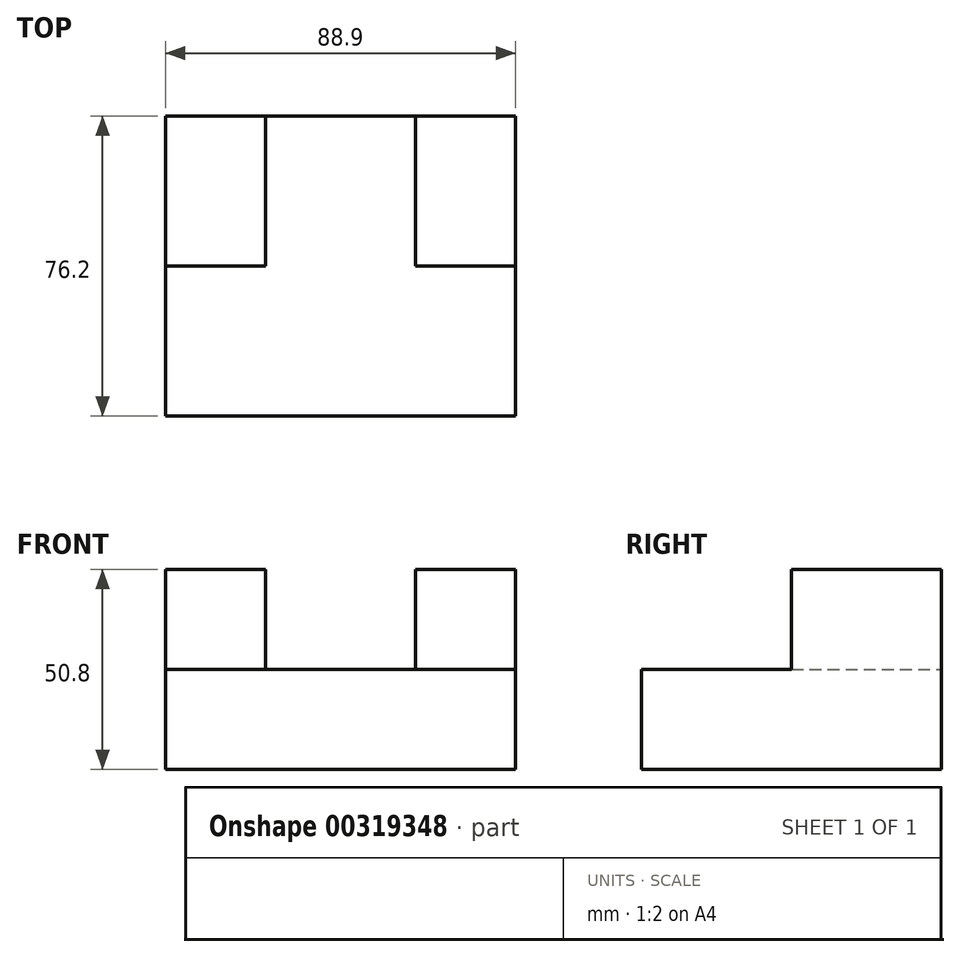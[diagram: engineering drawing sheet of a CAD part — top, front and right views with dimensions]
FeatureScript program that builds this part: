
annotation { "Feature Type Name" : "Feature", "Feature Type Description" : "" }
export const myFeature = defineFeature(function(context is Context, id is Id, definition is map)
    precondition{}
    {
        {
            var Q0;
            Q0=qCreatedBy(makeId("Front.planeOp"),FACE);
            var sketch = newSketch(context, id + "F0", { "sketchPlane" : qUnion([Q0])});
            skLineSegment(sketch, "E0", {"start": v(-56.68, -59.75) * mm, "end": v(32.22, -59.75) * mm});
            skLineSegment(sketch, "E1", {"start": v(32.22, -59.75) * mm, "end": v(32.22, -34.35) * mm});
            skLineSegment(sketch, "E2", {"start": v(-56.68, -59.75) * mm, "end": v(-56.68, -34.35) * mm});
            skLineSegment(sketch, "E3", {"start": v(-56.68, -34.35) * mm, "end": v(32.22, -34.35) * mm});
            skSolve(sketch);
        }
        {
            var Q0;
            Q0 = qSketchRegion(id + "F0", true);
            extrude(context, id + "F1", {"entities" : qUnion([Q0]), "depth" : 76.2 * mm});
        }
        {
            var Q0;
            Q0=makeQuery(id+"F1.opExtrude","SWEPT_FACE",FACE,{"disambiguationData":[OSD([sQuery(id+"F0.wireOp",EDGE,"E3")])]});
            var sketch = newSketch(context, id + "F2", { "sketchPlane" : qUnion([Q0])});
            skLineSegment(sketch, "E4", {"start": v(-56.68, 0) * mm, "end": v(-56.68, -38.1) * mm});
            skLineSegment(sketch, "E5", {"start": v(-56.68, -38.1) * mm, "end": v(-31.28, -38.1) * mm});
            skLineSegment(sketch, "E6", {"start": v(-31.28, -38.1) * mm, "end": v(-31.28, 0) * mm});
            skLineSegment(sketch, "E7", {"start": v(32.22, -38.1) * mm, "end": v(6.82, -38.1) * mm});
            skLineSegment(sketch, "E8", {"start": v(6.82, -38.1) * mm, "end": v(6.82, 0) * mm});
            skSolve(sketch);
        }
        {
            var Q0;
            {var subQ0=sQuery(id+"F2.wireOp",EDGE,"E4");Q0=makeQuery(id+"F2.imprint","IMPRINT",FACE,{"disambiguationData":[TD([[makeQuery(id+"F2.imprint","IMPRINT",EDGE,{"derivedFrom":subQ0}),-1.0]])]});}
            extrude(context, id + "F3", {"entities" : qUnion([Q0]), "operationType" : NewBodyOperationType.ADD, "depth" : 25.4 * mm});
        }
        {
            var Q0;
            Q0=makeQuery(id+"F1.opExtrude","SWEPT_FACE",FACE,{"disambiguationData":[OSD([sQuery(id+"F0.wireOp",EDGE,"E3")])]});
            var sketch = newSketch(context, id + "F4", { "sketchPlane" : qUnion([Q0])});
            skLineSegment(sketch, "E9", {"start": v(32.22, -38.1) * mm, "end": v(6.82, -38.1) * mm});
            skLineSegment(sketch, "E10", {"start": v(6.82, -38.1) * mm, "end": v(6.82, 0) * mm});
            skLineSegment(sketch, "E11", {"start": v(6.82, 0) * mm, "end": v(32.22, 0) * mm});
            skLineSegment(sketch, "E12", {"start": v(32.22, 0) * mm, "end": v(32.22, -38.1) * mm});
            skSolve(sketch);
        }
        {
            var Q0;
            Q0=makeQuery(id+"F4.imprint","IMPRINT",FACE,{"disambiguationData":[TD([[makeQuery(id+"F4.imprint","IMPRINT",EDGE,{"derivedFrom":sQuery(id+"F4.wireOp",EDGE,"E9")}),-1.0]])]});
            extrude(context, id + "F5", {"entities" : qUnion([Q0]), "operationType" : NewBodyOperationType.ADD, "depth" : 25.4 * mm});
        }
    });
